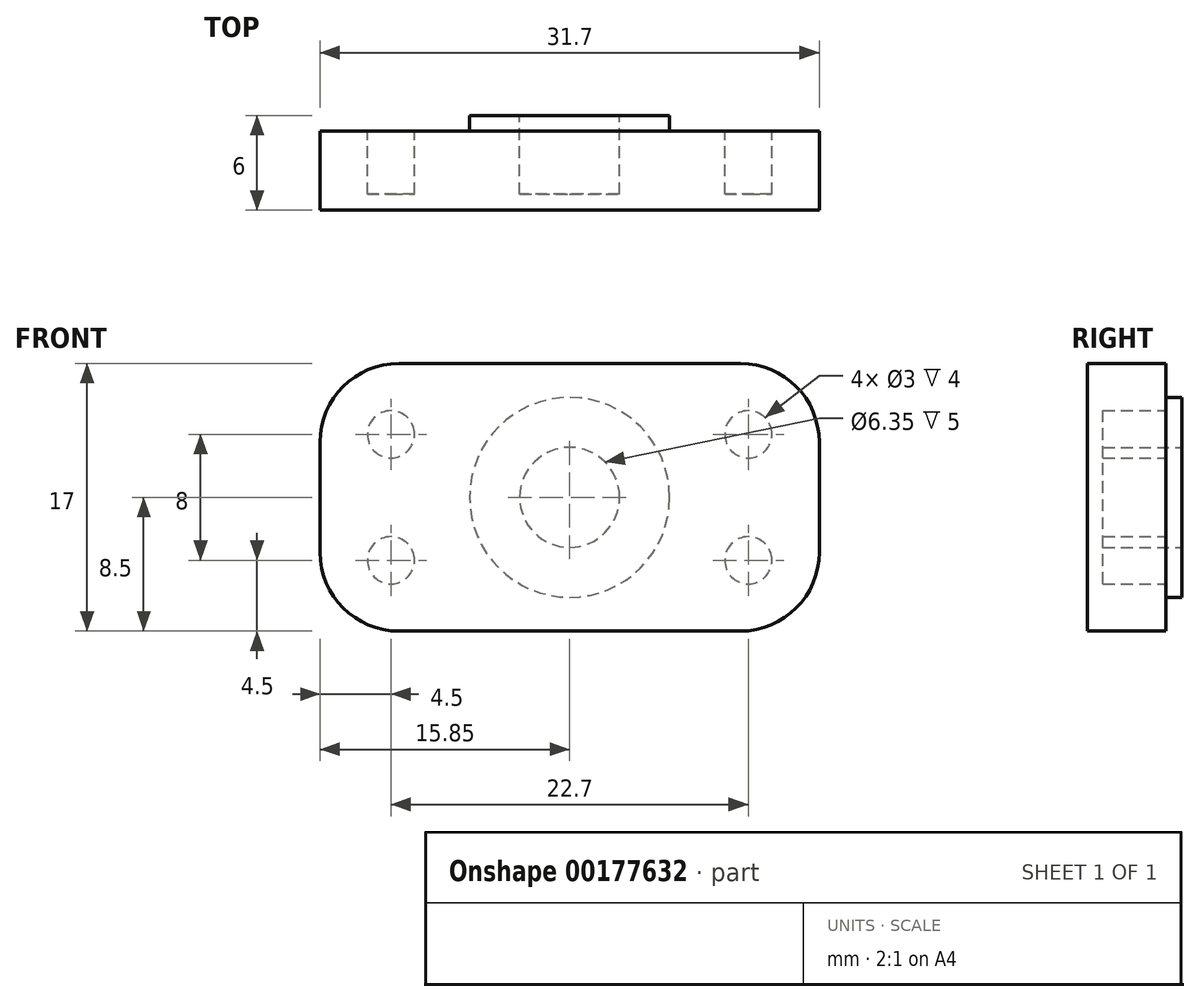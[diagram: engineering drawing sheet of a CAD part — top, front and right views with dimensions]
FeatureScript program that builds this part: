
annotation { "Feature Type Name" : "Feature", "Feature Type Description" : "" }
export const myFeature = defineFeature(function(context is Context, id is Id, definition is map)
    precondition{}
    {
        {
            var Q0;
            Q0=qCreatedBy(makeId("Front.planeOp"),FACE);
            var sketch = newSketch(context, id + "F0", { "sketchPlane" : qUnion([Q0])});
            skCircle(sketch, "E0", {"center": v(0, 0) * mm, "radius": 3.17 * mm});
            skCircle(sketch, "E1", {"center": v(0, 0) * mm, "radius": 6.35 * mm});
            skSolve(sketch);
        }
        {
            var Q0;
            Q0 = qSketchRegion(id + "F0", true);
            extrude(context, id + "F1", {"entities" : qUnion([Q0]), "depth" : 1 * mm});
        }
        {
            var Q0;
            Q0=makeQuery(id+"F1.opExtrude","CAP_FACE",FACE,{"disambiguationData":[OSD([sQuery(id+"F0.wireOp",EDGE,"E0"),sQuery(id+"F0.wireOp",EDGE,"E1")])],"isStart":false});
            var sketch = newSketch(context, id + "F2", { "sketchPlane" : qUnion([Q0])});
            skLineSegment(sketch, "E2.bottom", {"start": v(11.35, 11.35) * mm, "end": v(-11.35, 11.35) * mm, "construction": true});
            skLineSegment(sketch, "E2.top", {"start": v(11.35, -11.35) * mm, "end": v(-11.35, -11.35) * mm, "construction": true});
            skLineSegment(sketch, "E2.left", {"start": v(11.35, 11.35) * mm, "end": v(11.35, -11.35) * mm, "construction": true});
            skLineSegment(sketch, "E2.right", {"start": v(-11.35, 11.35) * mm, "end": v(-11.35, -11.35) * mm, "construction": true});
            skPoint(sketch, "E2.middle", {"position": v(0, 0) * mm});
            skCircle(sketch, "E3", {"center": v(-11.35, 4) * mm, "radius": 1.5 * mm});
            skCircle(sketch, "E4", {"center": v(-11.35, -4) * mm, "radius": 1.5 * mm});
            skCircle(sketch, "E5", {"center": v(11.35, -4) * mm, "radius": 1.5 * mm});
            skCircle(sketch, "E6", {"center": v(11.35, 4) * mm, "radius": 1.5 * mm});
            skLineSegment(sketch, "E7.bottom", {"start": v(15.85, 8.5) * mm, "end": v(-15.85, 8.5) * mm});
            skLineSegment(sketch, "E7.top", {"start": v(15.85, -8.5) * mm, "end": v(-15.85, -8.5) * mm});
            skLineSegment(sketch, "E7.left", {"start": v(15.85, 8.5) * mm, "end": v(15.85, -8.5) * mm});
            skLineSegment(sketch, "E7.right", {"start": v(-15.85, 8.5) * mm, "end": v(-15.85, -8.5) * mm});
            skSolve(sketch);
        }
        {
            var Q0;
            Q0 = qSketchRegion(id + "F2", true);
            extrude(context, id + "F3", {"entities" : qUnion([Q0]), "operationType" : NewBodyOperationType.ADD, "depth" : 5 * mm});
        }
        {
            var Q0;
            Q0=makeQuery(id+"F1.opExtrude","CAP_FACE",FACE,{"disambiguationData":[OSD([sQuery(id+"F0.wireOp",EDGE,"E0"),sQuery(id+"F0.wireOp",EDGE,"E1")])],"isStart":true});
            var sketch = newSketch(context, id + "F4", { "sketchPlane" : qUnion([Q0])});
            skCircle(sketch, "E8", {"center": v(0, 0) * mm, "radius": 3.17 * mm});
            skSolve(sketch);
        }
        {
            var Q0;
            Q0 = qSketchRegion(id + "F4", true);
            extrude(context, id + "F5", {"entities" : qUnion([Q0]), "operationType" : NewBodyOperationType.REMOVE, "oppositeDirection" : true, "depth" : 25 * mm});
        }
        {
            var Q0;
            Q0=makeQuery(id+"F3.opExtrude","CAP_FACE",FACE,{"disambiguationData":[OSD([sQuery(id+"F2.wireOp",EDGE,"E3"),sQuery(id+"F2.wireOp",EDGE,"E4"),sQuery(id+"F2.wireOp",EDGE,"E5"),sQuery(id+"F2.wireOp",EDGE,"E6"),sQuery(id+"F2.wireOp",EDGE,"E7.bottom"),sQuery(id+"F2.wireOp",EDGE,"E7.top"),sQuery(id+"F2.wireOp",EDGE,"E7.left"),sQuery(id+"F2.wireOp",EDGE,"E7.right")])],"isStart":false});
            var sketch = newSketch(context, id + "F6", { "sketchPlane" : qUnion([Q0])});
            skLineSegment(sketch, "E9.bottom", {"start": v(15.85, 8.5) * mm, "end": v(-15.85, 8.5) * mm});
            skLineSegment(sketch, "E9.top", {"start": v(15.85, -8.5) * mm, "end": v(-15.85, -8.5) * mm});
            skLineSegment(sketch, "E9.left", {"start": v(15.85, 8.5) * mm, "end": v(15.85, -8.5) * mm});
            skLineSegment(sketch, "E9.right", {"start": v(-15.85, 8.5) * mm, "end": v(-15.85, -8.5) * mm});
            skPoint(sketch, "E9.middle", {"position": v(0, 0) * mm});
            skSolve(sketch);
        }
        {
            var Q0;
            Q0 = qSketchRegion(id + "F6", true);
            extrude(context, id + "F7", {"entities" : qUnion([Q0]), "operationType" : NewBodyOperationType.ADD, "oppositeDirection" : true, "depth" : 1 * mm});
        }
        {
            var Q0;
            Q0=makeQuery(id+"F3.opExtrude","SWEPT_EDGE",EDGE,{"disambiguationData":[OSD([sQuery(id+"F2.wireOp",EDGE,"E7.top"),sQuery(id+"F2.wireOp",EDGE,"E7.right")])]});
            var Q1;
            Q1=makeQuery(id+"F3.opExtrude","SWEPT_EDGE",EDGE,{"disambiguationData":[OSD([sQuery(id+"F2.wireOp",EDGE,"E7.bottom"),sQuery(id+"F2.wireOp",EDGE,"E7.right")])]});
            var Q2;
            Q2=makeQuery(id+"F3.opExtrude","SWEPT_EDGE",EDGE,{"disambiguationData":[OSD([sQuery(id+"F2.wireOp",EDGE,"E7.bottom"),sQuery(id+"F2.wireOp",EDGE,"E7.left")])]});
            var Q3;
            Q3=makeQuery(id+"F3.opExtrude","SWEPT_EDGE",EDGE,{"disambiguationData":[OSD([sQuery(id+"F2.wireOp",EDGE,"E7.top"),sQuery(id+"F2.wireOp",EDGE,"E7.left")])]});
            fillet(context, id + "F8", {"entities" : qUnion([Q0, Q1, Q2, Q3]), "radius" : 5 * mm, "tangentPropagation" : true, "allowEdgeOverflow" : false});
        }
    });
